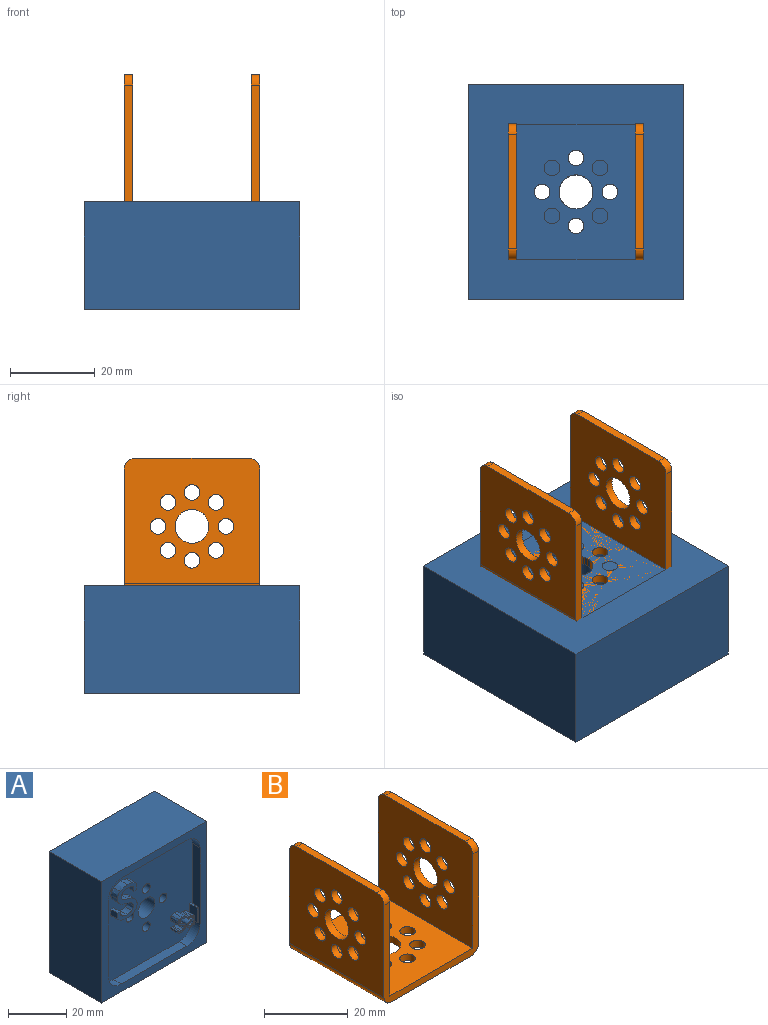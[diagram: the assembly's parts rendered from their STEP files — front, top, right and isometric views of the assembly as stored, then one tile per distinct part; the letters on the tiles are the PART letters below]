
ASSEMBLY  parts=2 mates=1
PART A: 111 faces, bbox 50.8x25.4x50.8 mm
  f0: cylinder r=1.85mm len=21.59mm, axis (0,1,0), area 251mm2, adj f5,f19
  f1: cylinder r=4mm len=21.59mm, axis (0,1,0), area 542.6mm2, adj f5,f19
  f2: cylinder r=1.85mm len=21.59mm, axis (0,1,0), area 251mm2, adj f5,f19
  f3: cylinder r=1.85mm len=21.59mm, axis (0,1,0), area 251mm2, adj f5,f19
  f4: cylinder r=1.85mm len=21.59mm, axis (0,1,0), area 251mm2, adj f5,f19
  f5: plane 50.8x50.8mm, normal (0,1,0), area 2487.4mm2, adj f0,f1,f2,f3,f4,f6,f7,f8
  f6: plane 50.8x25.4mm, normal (0,0,1), area 1290.3mm2, adj f5,f7,f9,f10
  f7: plane 50.8x25.4mm, normal (-1,0,0), area 1290.3mm2, adj f5,f6,f8,f10
  f8: plane 50.8x25.4mm, normal (0,0,-1), area 1290.3mm2, adj f5,f7,f9,f10
  f9: plane 50.8x25.4mm, normal (1,0,0), area 1290.3mm2, adj f5,f6,f8,f10
  f10: plane 50.8x50.8mm, normal (0,-1,0), area 644mm2, adj f6,f7,f8,f9,f11,f12,f13,f14
  f11: plane 31.7x3.81mm, normal (0,0,1), area 120.8mm2, adj f10,f12,f18,f19
  f12: cylinder r=6.35mm len=6.35mm, axis (0,-1,0), area 38mm2, adj f10,f11,f13,f19
  f13: plane 31.7x3.81mm, normal (-1,0,0), area 120.8mm2, adj f10,f12,f14,f19
  f14: cylinder r=6.35mm len=6.35mm, axis (0,-1,0), area 38mm2, adj f10,f13,f15,f19
  f15: plane 31.7x3.81mm, normal (0,0,-1), area 120.8mm2, adj f10,f14,f16,f19
  f16: cylinder r=6.35mm len=6.35mm, axis (0,-1,0), area 38mm2, adj f10,f15,f17,f19
  f17: plane 31.7x3.81mm, normal (1,0,0), area 120.8mm2, adj f10,f16,f18,f19
  f18: cylinder r=6.35mm len=6.35mm, axis (0,-1,0), area 38mm2, adj f10,f11,f17,f19
  f19: plane 44.4x44.4mm, normal (0,-1,0), area 1765.7mm2, adj f0,f1,f2,f3,f4,f11,f12,f13
  f20: plane 4.53x3.52mm, normal (0,-1,0), area 7.5mm2, adj f21,f22,f23,f24,f25,f26,f27,f28
  f21: plane 3.81x2.99mm, normal (1,0,0), area 11.4mm2, adj f19,f20,f22,f35
  f22: extruded ~3.81x1.12mm, area 4.6mm2, adj f19,f20,f21,f23
  f23: extruded ~3.81x1.16mm, area 4.7mm2, adj f19,f20,f22,f24
  f24: extruded ~3.81x0.77mm, area 3mm2, adj f19,f20,f23,f25
  f25: extruded ~3.81x0.71mm, area 2.9mm2, adj f19,f20,f24,f26
  f26: plane 3.81x0.51mm, normal (-0.93,0,-0.37), area 2.1mm2, adj f19,f20,f25,f27
  f27: extruded ~3.81x1.24mm, area 4.9mm2, adj f19,f20,f26,f36
  f28: plane 3.81x0.74mm, normal (-0.03,0,1), area 2.8mm2, adj f19,f20,f29,f38
  f29: extruded ~3.81x2.12mm, area 10.9mm2, adj f19,f20,f28,f30
  f30: extruded ~3.81x0.96mm, area 4mm2, adj f19,f20,f29,f31
  f31: extruded ~3.81x1.02mm, area 4.2mm2, adj f19,f20,f30,f32
  f32: extruded ~3.81x0.81mm, area 3.2mm2, adj f19,f20,f31,f33
  f33: extruded ~3.81x0.65mm, area 3.3mm2, adj f19,f20,f32,f39
  f34: plane 3.81x0.62mm, normal (-0.98,0,-0.21), area 2.4mm2, adj f19,f20,f35,f39
  f35: plane 3.81x0.49mm, normal (0,0,-1), area 1.9mm2, adj f19,f20,f21,f34
  f36: extruded ~3.81x0.71mm, area 2.9mm2, adj f19,f20,f27,f37
  f37: extruded ~3.81x0.76mm, area 3.1mm2, adj f19,f20,f36,f38
  f38: plane 3.81x0.27mm, normal (-1,0,0), area 1mm2, adj f19,f20,f28,f37
  f39: plane 3.81x0.03mm, normal (0,0,-1), area 0.1mm2, adj f19,f20,f33,f34
  f40: extruded ~3.81x0.61mm, area 2.5mm2, adj f20,f41,f47,f48
  f41: extruded ~3.81x0.97mm, area 4mm2, adj f20,f40,f42,f48
  f42: extruded ~3.81x0.95mm, area 4mm2, adj f20,f41,f43,f48
  f43: plane 3.81x0.4mm, normal (-1,0,0), area 1.5mm2, adj f20,f42,f44,f48
  f44: plane 3.81x0.66mm, normal (0.04,0,-1), area 2.5mm2, adj f20,f43,f45,f48
  f45: extruded ~3.81x1.14mm, area 4.5mm2, adj f20,f44,f46,f48
  f46: extruded ~3.81x0.68mm, area 3mm2, adj f20,f45,f47,f48
  f47: extruded ~3.81x0.55mm, area 2.3mm2, adj f20,f40,f46,f48
  f48: plane 2.15x1.69mm, normal (0,-1,0), area 2.9mm2, adj f40,f41,f42,f43,f44,f45,f46,f47
  f49: plane 6.01x3.68mm, normal (0,-1,0), area 7.9mm2, adj f50,f51,f52,f53,f54,f55,f56,f57
  f50: extruded ~3.81x1.41mm, area 5.5mm2, adj f19,f49,f51,f68
  f51: plane 3.81x0.59mm, normal (0.94,0,-0.34), area 2.4mm2, adj f19,f49,f50,f52
  f52: extruded ~3.81x1.6mm, area 6.3mm2, adj f19,f49,f51,f53
  f53: extruded ~3.81x1.34mm, area 5.4mm2, adj f19,f49,f52,f54
  f54: extruded ~3.81x1.08mm, area 4.7mm2, adj f19,f49,f53,f55
  f55: extruded ~3.81x1.04mm, area 4.3mm2, adj f19,f49,f54,f56
  f56: extruded ~3.81x1.17mm, area 5.2mm2, adj f19,f49,f55,f69
  f57: extruded ~3.81x1.27mm, area 5.6mm2, adj f19,f49,f63,f64
  f58: extruded ~3.81x0.78mm, area 3.1mm2, adj f19,f49,f59,f74
  f59: plane 3.81x0.66mm, normal (-1,0,0), area 2.5mm2, adj f19,f49,f58,f60
  f60: extruded ~3.81x1.6mm, area 6.2mm2, adj f19,f49,f59,f61
  f61: extruded ~3.81x1.52mm, area 6.1mm2, adj f19,f49,f60,f62
  f62: extruded ~3.81x1.2mm, area 5.3mm2, adj f19,f49,f61,f63
  f63: extruded ~3.81x0.98mm, area 4mm2, adj f19,f49,f57,f62
  f64: extruded ~3.81x0.81mm, area 3.4mm2, adj f19,f49,f57,f65
  f65: extruded ~3.81x0.38mm, area 2mm2, adj f19,f49,f64,f66
  f66: extruded ~3.81x0.5mm, area 2mm2, adj f19,f49,f65,f67
  f67: extruded ~3.81x0.64mm, area 2.8mm2, adj f19,f49,f66,f68
  f68: extruded ~3.81x0.84mm, area 3.4mm2, adj f19,f49,f50,f67
  f69: extruded ~3.81x0.87mm, area 3.6mm2, adj f19,f49,f56,f70
  f70: extruded ~3.81x0.41mm, area 2.1mm2, adj f19,f49,f69,f71
  f71: extruded ~3.81x0.5mm, area 2mm2, adj f19,f49,f70,f72
  f72: extruded ~3.81x0.72mm, area 3.2mm2, adj f19,f49,f71,f73
  f73: extruded ~3.81x1.02mm, area 4.1mm2, adj f19,f49,f72,f74
  f74: extruded ~3.81x0.84mm, area 3.2mm2, adj f19,f49,f58,f73
  f75: plane 6.22x0.66mm, normal (0,-1,0), area 4.1mm2, adj f76,f77,f78,f79
  f76: plane 3.81x0.66mm, normal (0,0,1), area 2.5mm2, adj f19,f75,f77,f79
  f77: plane 6.22x3.81mm, normal (-1,0,0), area 23.7mm2, adj f19,f75,f76,f78
  f78: plane 3.81x0.66mm, normal (0,0,-1), area 2.5mm2, adj f19,f75,f77,f79
  f79: plane 6.22x3.81mm, normal (1,0,0), area 23.7mm2, adj f19,f75,f76,f78
  f80: plane 3.18x1.38mm, normal (0,0,-1), area 4.4mm2, adj f19,f81,f109,f110
  f81: plane 3.18x2.51mm, normal (1,0,0), area 8mm2, adj f19,f80,f82,f110
  f82: extruded ~3.18x1.87mm, area 7.1mm2, adj f19,f81,f83,f110
  f83: extruded ~3.18x2.58mm, area 8.4mm2, adj f19,f82,f84,f110
  f84: extruded ~3.49x3.18mm, area 11.8mm2, adj f19,f83,f85,f110
  f85: extruded ~3.18x2.64mm, area 9.8mm2, adj f19,f84,f86,f110
  f86: extruded ~3.18x2.49mm, area 9.1mm2, adj f19,f85,f87,f110
  f87: extruded ~3.35x3.18mm, area 11.7mm2, adj f19,f86,f88,f110
  f88: extruded ~3.18x2.46mm, area 8.6mm2, adj f19,f87,f89,f110
  f89: extruded ~3.18x1.55mm, area 5.6mm2, adj f19,f88,f90,f110
  f90: extruded ~3.18x1.59mm, area 5.9mm2, adj f19,f89,f91,f110
  f91: extruded ~3.18x2.18mm, area 7.3mm2, adj f19,f90,f92,f110
  f92: extruded ~3.18x1.75mm, area 5.7mm2, adj f19,f91,f93,f110
  f93: extruded ~3.18x1.26mm, area 4.6mm2, adj f19,f92,f94,f110
  f94: plane 3.18x1.94mm, normal (0.98,0,0.18), area 6.2mm2, adj f19,f93,f95,f110
  f95: plane 3.18x1.37mm, normal (0,0,1), area 4.4mm2, adj f19,f94,f96,f110
  f96: plane 3.18x2.51mm, normal (-1,0,0), area 8mm2, adj f19,f95,f97,f110
  f97: extruded ~3.18x1.97mm, area 7.6mm2, adj f19,f96,f98,f110
  f98: extruded ~3.18x2.77mm, area 9mm2, adj f19,f97,f99,f110
  f99: extruded ~3.48x3.18mm, area 11.7mm2, adj f19,f98,f100,f110
  f100: extruded ~3.18x2.62mm, area 9.7mm2, adj f19,f99,f101,f110
  f101: extruded ~3.18x2.55mm, area 9.1mm2, adj f19,f100,f102,f110
  f102: extruded ~3.24x3.18mm, area 11.5mm2, adj f19,f101,f103,f110
  f103: extruded ~3.18x2.56mm, area 8.8mm2, adj f19,f102,f104,f110
  f104: extruded ~3.18x1.47mm, area 5.5mm2, adj f19,f103,f105,f110
  f105: extruded ~3.18x1.61mm, area 5.9mm2, adj f19,f104,f106,f110
  f106: extruded ~3.18x2.23mm, area 7.5mm2, adj f19,f105,f107,f110
  f107: extruded ~3.18x1.61mm, area 5.2mm2, adj f19,f106,f108,f110
  f108: extruded ~3.18x1.11mm, area 4mm2, adj f19,f107,f109,f110
  f109: plane 3.18x1.93mm, normal (-0.98,0,-0.18), area 6.2mm2, adj f19,f80,f108,f110
  f110: plane 13.88x9.55mm, normal (0,-1,0), area 55.2mm2, adj f80,f81,f82,f83,f84,f85,f86,f87
PART B: 43 faces, bbox 32x32x32 mm
  f0: plane 32x29.5mm, normal (-1,0,0), area 805mm2, adj f1,f3,f5,f10,f11,f12,f13,f14
  f1: plane 27x2mm, normal (0,0,1), area 54mm2, adj f0,f7,f38,f39
  f2: plane 27x2mm, normal (0,0,1), area 54mm2, adj f6,f9,f41,f42
  f3: plane 32x29.5mm, normal (0,1,0), area 171.3mm2, adj f0,f4,f6,f7,f8,f9,f37,f39
  f4: plane 32x27mm, normal (0,0,-1), area 727.7mm2, adj f3,f5,f19,f20,f21,f22,f23,f24
  f5: plane 32x29.5mm, normal (0,-1,0), area 171.3mm2, adj f0,f4,f6,f7,f8,f9,f37,f38
  f6: plane 32x29.5mm, normal (1,0,0), area 805mm2, adj f2,f3,f5,f28,f29,f30,f31,f32
  f7: plane 32x30mm, normal (1,0,0), area 821mm2, adj f1,f3,f5,f8,f10,f11,f12,f13
  f8: plane 32x28mm, normal (0,0,1), area 759.7mm2, adj f3,f5,f7,f9,f19,f20,f21,f22
  f9: plane 32x30mm, normal (-1,0,0), area 821mm2, adj f2,f3,f5,f8,f28,f29,f30,f31
  f10: cylinder r=4mm len=8mm, axis (-1,0,0), area 50.3mm2, adj f0,f7
  f11: cylinder r=1.85mm len=3.7mm, axis (-1,0,0), area 23.2mm2, adj f0,f7
  f12: cylinder r=1.85mm len=3.7mm, axis (-1,0,0), area 23.2mm2, adj f0,f7
  f13: cylinder r=1.85mm len=3.7mm, axis (-1,0,0), area 23.2mm2, adj f0,f7
  f14: cylinder r=1.85mm len=3.7mm, axis (-1,0,0), area 23.2mm2, adj f0,f7
  f15: cylinder r=1.85mm len=3.7mm, axis (-1,0,0), area 23.2mm2, adj f0,f7
  f16: cylinder r=1.85mm len=3.7mm, axis (-1,0,0), area 23.2mm2, adj f0,f7
  f17: cylinder r=1.85mm len=3.7mm, axis (-1,0,0), area 23.2mm2, adj f0,f7
  f18: cylinder r=1.85mm len=3.7mm, axis (-1,0,0), area 23.2mm2, adj f0,f7
  f19: cylinder r=1.85mm len=3.7mm, axis (0,0,1), area 23.2mm2, adj f4,f8
  f20: cylinder r=1.85mm len=3.7mm, axis (0,0,1), area 23.2mm2, adj f4,f8
  f21: cylinder r=1.85mm len=3.7mm, axis (0,0,1), area 23.2mm2, adj f4,f8
  f22: cylinder r=1.85mm len=3.7mm, axis (0,0,1), area 23.2mm2, adj f4,f8
  f23: cylinder r=1.85mm len=3.7mm, axis (0,0,1), area 23.2mm2, adj f4,f8
  f24: cylinder r=1.85mm len=3.7mm, axis (0,0,1), area 23.2mm2, adj f4,f8
  f25: cylinder r=1.85mm len=3.7mm, axis (0,0,1), area 23.2mm2, adj f4,f8
  f26: cylinder r=1.85mm len=3.7mm, axis (0,0,1), area 23.2mm2, adj f4,f8
  f27: cylinder r=4mm len=8mm, axis (0,0,-1), area 50.3mm2, adj f4,f8
  f28: cylinder r=4mm len=8mm, axis (1,0,0), area 50.3mm2, adj f6,f9
  f29: cylinder r=1.85mm len=3.7mm, axis (1,0,0), area 23.2mm2, adj f6,f9
  f30: cylinder r=1.85mm len=3.7mm, axis (1,0,0), area 23.2mm2, adj f6,f9
  f31: cylinder r=1.85mm len=3.7mm, axis (1,0,0), area 23.2mm2, adj f6,f9
  f32: cylinder r=1.85mm len=3.7mm, axis (1,0,0), area 23.2mm2, adj f6,f9
  f33: cylinder r=1.85mm len=3.7mm, axis (1,0,0), area 23.2mm2, adj f6,f9
  f34: cylinder r=1.85mm len=3.7mm, axis (1,0,0), area 23.2mm2, adj f6,f9
  f35: cylinder r=1.85mm len=3.7mm, axis (1,0,0), area 23.2mm2, adj f6,f9
  f36: cylinder r=1.85mm len=3.7mm, axis (1,0,0), area 23.2mm2, adj f6,f9
  f37: cylinder r=2.5mm len=32mm, axis (0,-1,0), area 125.7mm2, adj f0,f3,f4,f5
  f38: cylinder r=2.5mm len=2.5mm, axis (1,0,0), area 7.9mm2, adj f0,f1,f5,f7
  f39: cylinder r=2.5mm len=2.5mm, axis (1,0,0), area 7.9mm2, adj f0,f1,f3,f7
  f40: cylinder r=2.5mm len=32mm, axis (0,1,0), area 125.7mm2, adj f3,f4,f5,f6
  f41: cylinder r=2.5mm len=2.5mm, axis (1,0,0), area 7.9mm2, adj f2,f5,f6,f9
  f42: cylinder r=2.5mm len=2.5mm, axis (1,0,0), area 7.9mm2, adj f2,f3,f6,f9
PLACE A rot(axis=(1,0,0),90deg) t=(-41.39,66.82,15.77)mm
PLACE B t=(-59.88,48.96,13.77)mm
MATE fastened A.f1 <-> B.f27  axis (0,0,1) through (-59.88,48.96,15.77)mm
